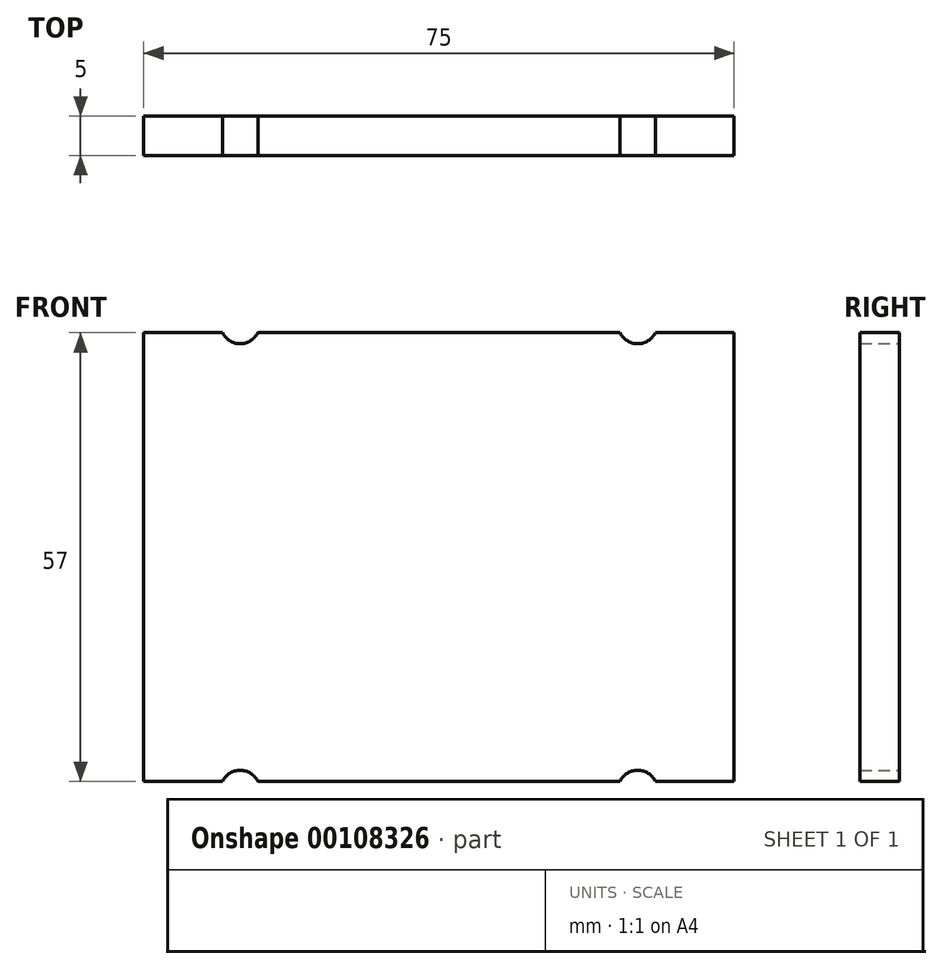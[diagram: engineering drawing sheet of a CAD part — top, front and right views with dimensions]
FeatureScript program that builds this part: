
annotation { "Feature Type Name" : "Feature", "Feature Type Description" : "" }
export const myFeature = defineFeature(function(context is Context, id is Id, definition is map)
    precondition{}
    {
        {
            var Q0;
            Q0=qCreatedBy(makeId("Front.planeOp"),FACE);
            var sketch = newSketch(context, id + "F0", { "sketchPlane" : qUnion([Q0])});
            skLineSegment(sketch, "E0.bottom", {"start": v(-37.5, 28.5) * mm, "end": v(-27.5, 28.5) * mm});
            skLineSegment(sketch, "E0.top", {"start": v(-37.5, -28.5) * mm, "end": v(-27.5, -28.5) * mm});
            skLineSegment(sketch, "E0.left", {"start": v(-37.5, 28.5) * mm, "end": v(-37.5, -28.5) * mm});
            skLineSegment(sketch, "E0.right", {"start": v(37.5, 28.5) * mm, "end": v(37.5, -28.5) * mm});
            skPoint(sketch, "E0.middle", {"position": v(0, 0) * mm});
            skArc(sketch, "E1", {"start": v(-27.5, 28.5) * mm, "mid": v(-24.7, 27.15) * mm, "end": v(-22.75, 29.59) * mm});
            skArc(sketch, "E2.MirrorC", {"start": v(27.5, 28.5) * mm, "mid": v(24.7, 27.15) * mm, "end": v(22.75, 29.59) * mm});
            skLineSegment(sketch, "E3.MirrorCS", {"start": v(37.5, 28.5) * mm, "end": v(27.5, 28.5) * mm});
            skArc(sketch, "E4.MirrorC", {"start": v(27.5, -28.5) * mm, "mid": v(24.7, -27.15) * mm, "end": v(22.75, -29.59) * mm});
            skArc(sketch, "E5.MirrorC", {"start": v(-27.5, -28.5) * mm, "mid": v(-24.7, -27.15) * mm, "end": v(-22.75, -29.59) * mm});
            skLineSegment(sketch, "E6.MirrorCS", {"start": v(37.5, -28.5) * mm, "end": v(27.5, -28.5) * mm});
            skLineSegment(sketch, "E7.trimOffspring", {"start": v(-27.5, 28.5) * mm, "end": v(-37.5, 28.5) * mm});
            skLineSegment(sketch, "E8.trimOffspring", {"start": v(-23, 28.5) * mm, "end": v(23, 28.5) * mm});
            skLineSegment(sketch, "E9.MirrorCS", {"start": v(27.5, 28.5) * mm, "end": v(37.5, 28.5) * mm});
            skLineSegment(sketch, "E10.MirrorCS", {"start": v(23, 28.5) * mm, "end": v(-23, 28.5) * mm});
            skLineSegment(sketch, "E11.trimOffspring", {"start": v(-23, -28.5) * mm, "end": v(23, -28.5) * mm});
            skLineSegment(sketch, "E12.trimOffspring", {"start": v(27.5, -28.5) * mm, "end": v(37.5, -28.5) * mm});
            skLineSegment(sketch, "E13.trimOffspring", {"start": v(23, -28.5) * mm, "end": v(-23, -28.5) * mm});
            skLineSegment(sketch, "E14.trimOffspring", {"start": v(-27.5, -28.5) * mm, "end": v(-37.5, -28.5) * mm});
            skSolve(sketch);
        }
        {
            var Q0;
            Q0 = qSketchRegion(id + "F0", true);
            extrude(context, id + "F1", {"entities" : qUnion([Q0]), "depth" : 5 * mm});
        }
    });
